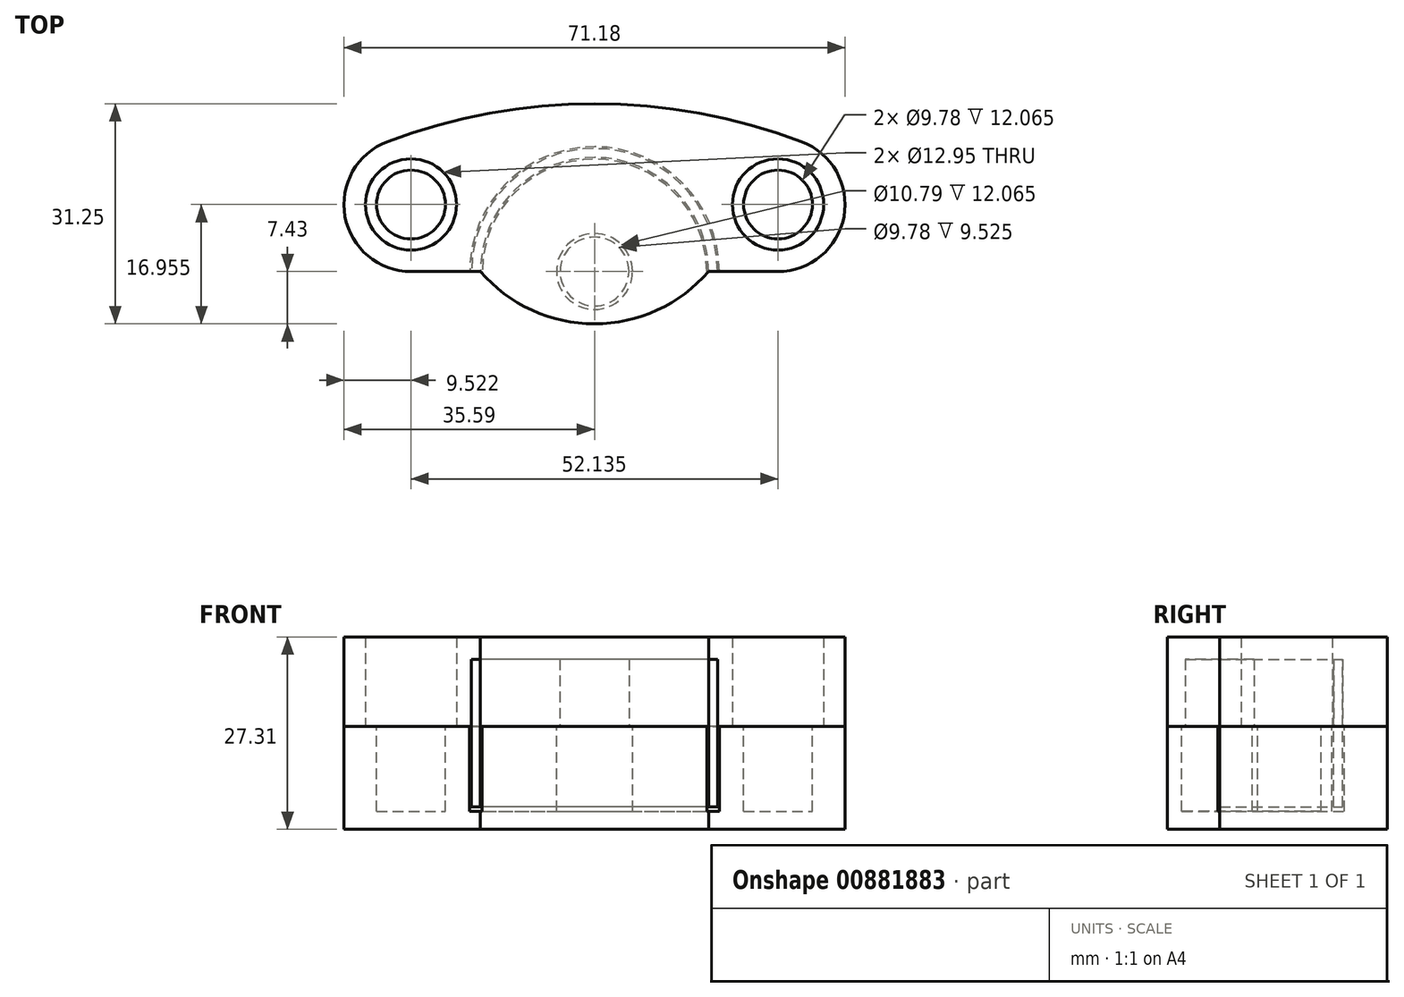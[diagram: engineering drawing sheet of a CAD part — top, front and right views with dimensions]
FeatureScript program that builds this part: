
annotation { "Feature Type Name" : "Feature", "Feature Type Description" : "" }
export const myFeature = defineFeature(function(context is Context, id is Id, definition is map)
    precondition{}
    {
        {
            var Q0;
            Q0=qCreatedBy(makeId("Top.planeOp"),FACE);
            var sketch = newSketch(context, id + "F0", { "sketchPlane" : qUnion([Q0])});
            skArc(sketch, "E0", {"start": v(17.47, 0) * mm, "mid": v(0, 17.47) * mm, "end": v(-17.47, 0) * mm});
            skLineSegment(sketch, "E1", {"start": v(-17.47, 0) * mm, "end": v(-26.07, 0) * mm});
            skCircle(sketch, "E2", {"center": v(-26.07, 9.53) * mm, "radius": 6.48 * mm});
            skArc(sketch, "E3", {"start": v(-29.44, 18.43) * mm, "mid": v(-35.44, 7.81) * mm, "end": v(-26.07, 0) * mm});
            skCircle(sketch, "E4", {"center": v(26.07, 9.53) * mm, "radius": 6.48 * mm});
            skArc(sketch, "E5", {"start": v(26.07, 0) * mm, "mid": v(35.44, 7.81) * mm, "end": v(29.44, 18.43) * mm});
            skLineSegment(sketch, "E6", {"start": v(17.47, 0) * mm, "end": v(26.07, 0) * mm});
            skArc(sketch, "E7", {"start": v(29.44, 18.43) * mm, "mid": v(0, 23.82) * mm, "end": v(-29.44, 18.43) * mm});
            skArc(sketch, "E8.0", {"start": v(16.2, 0) * mm, "mid": v(0, 16.2) * mm, "end": v(-16.2, 0) * mm});
            skCircle(sketch, "E9", {"center": v(0, 0) * mm, "radius": 4.89 * mm});
            skArc(sketch, "E10", {"start": v(-16.2, 0) * mm, "mid": v(0, -7.43) * mm, "end": v(16.2, 0) * mm});
            skSolve(sketch);
        }
        {
            var Q0;
            Q0 = qSketchRegion(id + "F0", true);
            extrude(context, id + "F1", {"entities" : qUnion([Q0]), "depth" : 12.7 * mm, "offsetDistance" : 25.4 * mm});
        }
        {
            var Q0;
            Q0=makeQuery(id+"F1.opExtrude","CAP_FACE",FACE,{"disambiguationData":[OSD([sQuery(id+"F0.wireOp",EDGE,"E0"),sQuery(id+"F0.wireOp",EDGE,"E1"),sQuery(id+"F0.wireOp",EDGE,"E2"),sQuery(id+"F0.wireOp",EDGE,"E3"),sQuery(id+"F0.wireOp",EDGE,"E4"),sQuery(id+"F0.wireOp",EDGE,"E5"),sQuery(id+"F0.wireOp",EDGE,"E6"),sQuery(id+"F0.wireOp",EDGE,"E7")])],"isStart":false});
            var sketch = newSketch(context, id + "F2", { "sketchPlane" : qUnion([Q0])});
            skLineSegment(sketch, "E11", {"start": v(-17.47, 0) * mm, "end": v(-16.2, 0) * mm});
            skLineSegment(sketch, "E12", {"start": v(16.2, 0) * mm, "end": v(17.47, 0) * mm});
            skPoint(sketch, "E13.0.3.start.orphan", {"position": v(-29.44, 18.43) * mm});
            skPoint(sketch, "E13.0.1.end.orphan", {"position": v(29.44, 18.43) * mm});
            skPoint(sketch, "E13.0.0.end.orphan", {"position": v(26.07, 0) * mm});
            skPoint(sketch, "E13.0.4.start.orphan", {"position": v(-26.07, 0) * mm});
            skArc(sketch, "E14.0", {"start": v(17.47, 0) * mm, "mid": v(0, 17.47) * mm, "end": v(-17.47, 0) * mm});
            skArc(sketch, "E15.0", {"start": v(16.2, 0) * mm, "mid": v(0, 16.2) * mm, "end": v(-16.2, 0) * mm});
            skCircle(sketch, "E16.0", {"center": v(0, 0) * mm, "radius": 4.89 * mm});
            skSolve(sketch);
        }
        {
            var Q0;
            Q0 = qSketchRegion(id + "F2", true);
            extrude(context, id + "F3", {"entities" : qUnion([Q0]), "operationType" : NewBodyOperationType.ADD, "oppositeDirection" : true, "depth" : 3.17 * mm, "offsetDistance" : 25.4 * mm});
        }
        {
            var Q0;
            Q0=makeQuery(id+"F3.opExtrude","CAP_FACE",FACE,{"disambiguationData":[OSD([sQuery(id+"F2.wireOp",EDGE,"E11"),sQuery(id+"F2.wireOp",EDGE,"E12"),sQuery(id+"F2.wireOp",EDGE,"E14.0"),sQuery(id+"F2.wireOp",EDGE,"E15.0")])],"isStart":false});
            var sketch = newSketch(context, id + "F4", { "sketchPlane" : qUnion([Q0])});
            skArc(sketch, "E17.0", {"start": v(17.47, 0) * mm, "mid": v(0, -17.47) * mm, "end": v(-17.47, 0) * mm});
            skArc(sketch, "E18.0", {"start": v(16.2, 0) * mm, "mid": v(0, -16.2) * mm, "end": v(-16.2, 0) * mm});
            skLineSegment(sketch, "E19", {"start": v(-17.47, 0) * mm, "end": v(-16.2, 0) * mm});
            skLineSegment(sketch, "E20", {"start": v(16.2, 0) * mm, "end": v(17.47, 0) * mm});
            skSolve(sketch);
        }
        {
            var Q0;
            Q0 = qSketchRegion(id + "F4", true);
            extrude(context, id + "F5", {"entities" : qUnion([Q0]), "depth" : 20.95 * mm, "offsetDistance" : 25.4 * mm});
        }
        {
            var Q0;
            Q0=makeQuery(id+"F1.opExtrude","CAP_FACE",FACE,{"disambiguationData":[OSD([sQuery(id+"F0.wireOp",EDGE,"E0"),sQuery(id+"F0.wireOp",EDGE,"E1"),sQuery(id+"F0.wireOp",EDGE,"E2"),sQuery(id+"F0.wireOp",EDGE,"E3"),sQuery(id+"F0.wireOp",EDGE,"E4"),sQuery(id+"F0.wireOp",EDGE,"E5"),sQuery(id+"F0.wireOp",EDGE,"E6"),sQuery(id+"F0.wireOp",EDGE,"E7")])],"isStart":true});
            var sketch = newSketch(context, id + "F6", { "sketchPlane" : qUnion([Q0])});
            skLineSegment(sketch, "E21.0.0", {"start": v(26.07, 0) * mm, "end": v(17.47, 0) * mm});
            skArc(sketch, "E21.0.1", {"start": v(17.47, 0) * mm, "mid": v(0, -17.47) * mm, "end": v(-17.47, 0) * mm, "construction": true});
            skLineSegment(sketch, "E21.0.2", {"start": v(-17.47, 0) * mm, "end": v(-26.07, 0) * mm});
            skArc(sketch, "E21.0.3", {"start": v(-26.07, 0) * mm, "mid": v(-35.44, -7.81) * mm, "end": v(-29.44, -18.43) * mm});
            skArc(sketch, "E21.0.4", {"start": v(-29.44, -18.43) * mm, "mid": v(0, -23.82) * mm, "end": v(29.44, -18.43) * mm});
            skArc(sketch, "E21.0.5", {"start": v(29.44, -18.43) * mm, "mid": v(35.44, -7.81) * mm, "end": v(26.07, 0) * mm});
            skArc(sketch, "E22.0.0", {"start": v(-16.2, 0) * mm, "mid": v(0, -16.2) * mm, "end": v(16.2, 0) * mm, "construction": true});
            skArc(sketch, "E22.0.1", {"start": v(16.2, 0) * mm, "mid": v(0, 7.43) * mm, "end": v(-16.2, 0) * mm});
            skCircle(sketch, "E23.0", {"center": v(0, 0) * mm, "radius": 5.4 * mm});
            skCircle(sketch, "E24", {"center": v(-26.07, -9.53) * mm, "radius": 4.89 * mm});
            skCircle(sketch, "E25", {"center": v(26.07, -9.53) * mm, "radius": 4.89 * mm});
            skArc(sketch, "E26.0", {"start": v(17.72, 0) * mm, "mid": v(0, -17.72) * mm, "end": v(-17.72, 0) * mm});
            skArc(sketch, "E27.0", {"start": v(-15.94, 0) * mm, "mid": v(0, -15.94) * mm, "end": v(15.94, 0) * mm});
            skLineSegment(sketch, "E28", {"start": v(-15.94, 0) * mm, "end": v(-15.94, 0.29) * mm});
            skLineSegment(sketch, "E29", {"start": v(15.94, 0) * mm, "end": v(15.94, 0.29) * mm});
            skSolve(sketch);
        }
        {
            var Q0;
            Q0 = qSketchRegion(id + "F6", true);
            extrude(context, id + "F7", {"entities" : qUnion([Q0]), "depth" : 14.6 * mm, "offsetDistance" : 25.4 * mm});
        }
        {
            var Q0;
            Q0=makeQuery(id+"F7.opExtrude","CAP_FACE",FACE,{"disambiguationData":[OSD([sQuery(id+"F6.wireOp",EDGE,"E21.0.0"),sQuery(id+"F6.wireOp",EDGE,"E21.0.1"),sQuery(id+"F6.wireOp",EDGE,"E21.0.2"),sQuery(id+"F6.wireOp",EDGE,"E21.0.3"),sQuery(id+"F6.wireOp",EDGE,"E21.0.4"),sQuery(id+"F6.wireOp",EDGE,"E21.0.5"),sQuery(id+"F6.wireOp",EDGE,"E24"),sQuery(id+"F6.wireOp",EDGE,"E25")])],"isStart":false});
            var sketch = newSketch(context, id + "F8", { "sketchPlane" : qUnion([Q0])});
            skLineSegment(sketch, "E30.0.0", {"start": v(26.07, 0) * mm, "end": v(26.07, 0) * mm});
            skLineSegment(sketch, "E30.0.2", {"start": v(-17.47, 0) * mm, "end": v(-26.07, 0) * mm});
            skArc(sketch, "E30.0.3", {"start": v(-26.07, 0) * mm, "mid": v(-35.44, -7.81) * mm, "end": v(-29.44, -18.43) * mm});
            skArc(sketch, "E30.0.4", {"start": v(-29.44, -18.43) * mm, "mid": v(0, -23.82) * mm, "end": v(29.44, -18.43) * mm});
            skArc(sketch, "E30.0.5", {"start": v(29.44, -18.43) * mm, "mid": v(35.44, -7.81) * mm, "end": v(26.07, 0) * mm});
            skArc(sketch, "E31.0.1", {"start": v(16.2, 0) * mm, "mid": v(0, 7.43) * mm, "end": v(-16.2, 0) * mm});
            skLineSegment(sketch, "E32", {"start": v(-17.47, 0) * mm, "end": v(-16.2, 0) * mm});
            skLineSegment(sketch, "E33", {"start": v(16.2, 0) * mm, "end": v(26.07, 0) * mm});
            skSolve(sketch);
        }
        {
            var Q0;
            Q0 = qSketchRegion(id + "F8", true);
            extrude(context, id + "F9", {"entities" : qUnion([Q0]), "operationType" : NewBodyOperationType.ADD, "oppositeDirection" : true, "depth" : 2.54 * mm, "offsetDistance" : 25.4 * mm});
        }
    });
